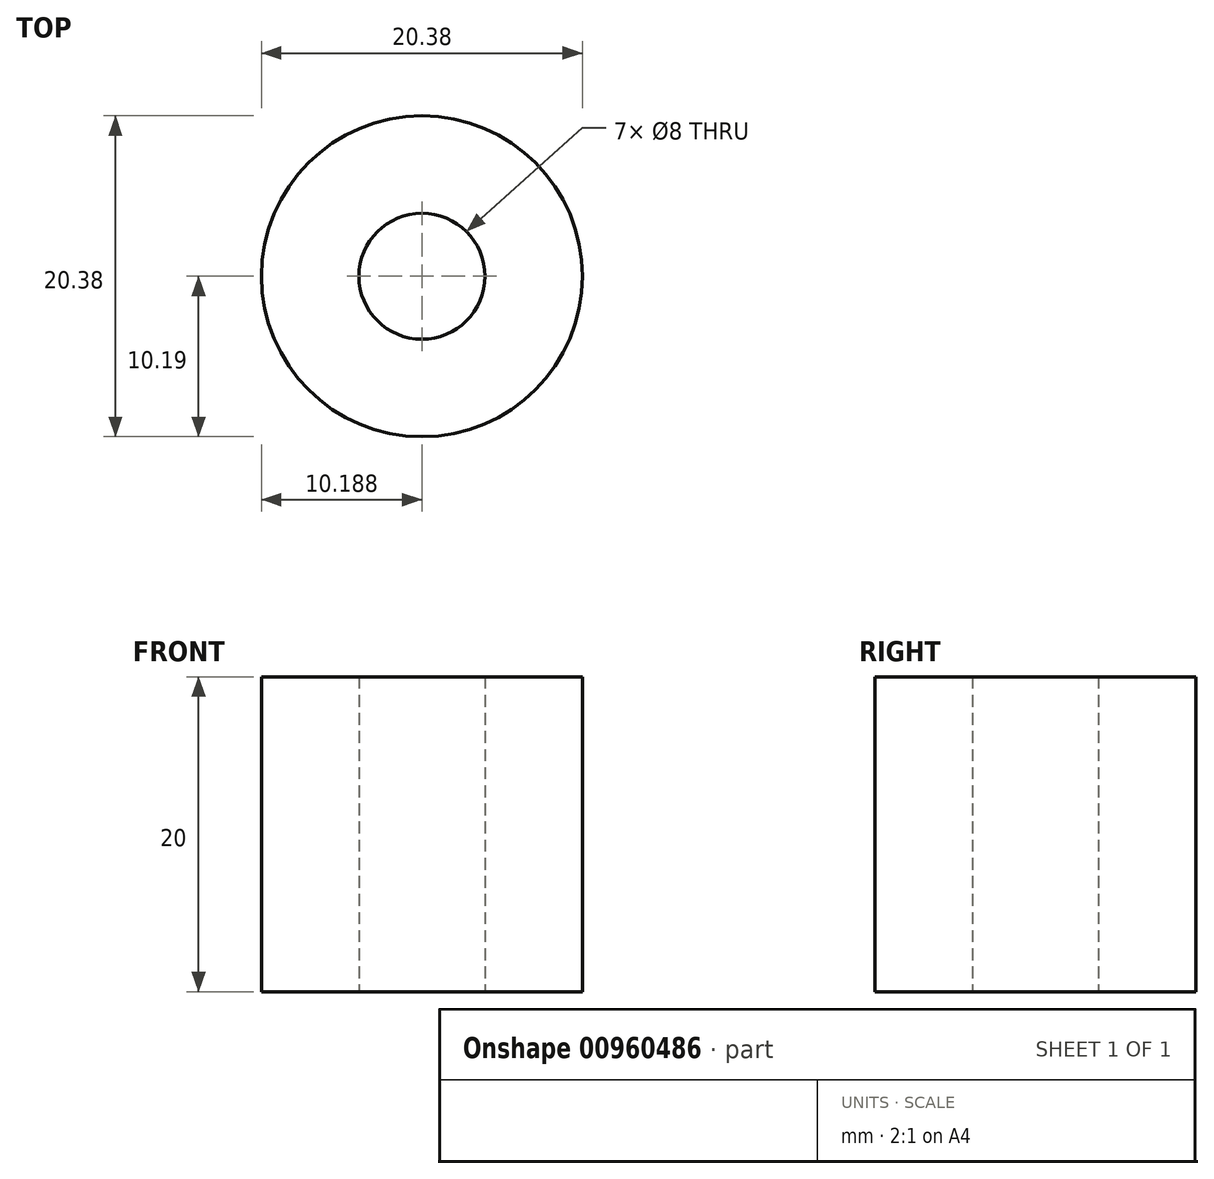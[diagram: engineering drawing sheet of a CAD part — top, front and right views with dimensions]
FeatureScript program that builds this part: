
annotation { "Feature Type Name" : "Feature", "Feature Type Description" : "" }
export const myFeature = defineFeature(function(context is Context, id is Id, definition is map)
    precondition{}
    {
        {
            var Q0;
            Q0=qCreatedBy(makeId("Top.planeOp"),FACE);
            var sketch = newSketch(context, id + "F0", { "sketchPlane" : qUnion([Q0])});
            skLineSegment(sketch, "E0.bottom", {"start": v(45.8, -19.3) * mm, "end": v(-45.8, -19.3) * mm});
            skLineSegment(sketch, "E0.top", {"start": v(45.8, 19.3) * mm, "end": v(-45.8, 19.3) * mm});
            skLineSegment(sketch, "E0.left", {"start": v(45.8, -19.3) * mm, "end": v(45.8, 19.3) * mm});
            skLineSegment(sketch, "E0.right", {"start": v(-45.8, -19.3) * mm, "end": v(-45.8, 19.3) * mm});
            skPoint(sketch, "E0.middle", {"position": v(0, 0) * mm});
            skCircle(sketch, "E1", {"center": v(-28.33, -0.29) * mm, "radius": 4 * mm});
            skPoint(sketch, "E1.first.point", {"position": v(-32.32, 0) * mm});
            skPoint(sketch, "E1.second.point", {"position": v(-24.34, 0) * mm});
            skPoint(sketch, "E1.third.point", {"position": v(-29.95, 3.37) * mm});
            skCircle(sketch, "E2", {"center": v(-28.33, -0.29) * mm, "radius": 10.2 * mm});
            skSolve(sketch);
        }
        {
            var Q0;
            Q0=makeQuery(id+"F0.imprint","IMPRINT",FACE,{"disambiguationData":[TD([[makeQuery(id+"F0.imprint","IMPRINT",EDGE,{"derivedFrom":sQuery(id+"F0.wireOp",EDGE,"E1")}),-1.0]])]});
            extrude(context, id + "F1", {"entities" : qUnion([Q0]), "endBound" : BoundingType.SYMMETRIC, "depth" : 20 * mm, "offsetDistance" : 25.4 * mm});
        }
    });
